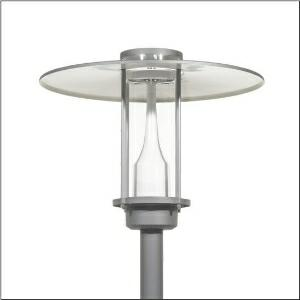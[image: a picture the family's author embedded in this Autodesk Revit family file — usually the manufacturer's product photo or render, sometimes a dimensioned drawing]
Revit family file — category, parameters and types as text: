
# Revit family: city-light_plus_iq___pl1_2s_5xa5275rf14h_8fc2
name_source: partatom
category: Lighting Fixtures
units: mm (PartAtom-declared; Revit-internal decimal feet)

## family parameters
Cut with Voids When Loaded = No
Host = Face
Light Source = No
Part Type = Normal
Room Calculation Point = No
Round Connector Dimension = Use Diameter
Shared = No

## types (1)
- --- (1 x LED, 2840 lm, 18.5 W, 4000K)
    Apparent Load = 19 VA
    CIE Flux Codes = 23 63 93 97 100
    Color Rendering = 70
    Color Temperature = 4000K
    Default Elevation = 1800 mm
    Description = City-Light Plus iQ, mast luminaire, Module 540 iQ-SR, primary light control with 3 zone facetted reflector, of plastic, silver coated, highly specular, structured, primary optical cover: cover, of PMMA, transparent, light distribution: PL1.2s, light emission: direct distribution, primary light characteristic: symmetric, installation type: post-top, LED, High Power LED, rated luminous flux: 2.840lm, luminous efficacy: 153lm/W, light colour: 740, colour temperature: 4000K, control gear: iQ Street-Remote, control: pre-setting: logarithmic dimming characteristic, Street-Remote, Auto-Match, Temp-Guard, Lumen-Switch, Night-Set, Smart-Wire, Light-Fading, Desk-Remote (wireless, voltage-free reading and setting of iQ features in the workshop via application-optimized NFC function/RFID function), optimised constant luminous flux control (CLO 2.0), with terminal, 6-pole, max. 2.5mm², mains connection: 230..240V, AC, 50/60Hz, start of lifetime: 19W, end of service life: 20W, reduction: 9W, luminaire housing, upper part, of glass-fibre reinforced polyester, coated, Siteco® metallic grey (DB 702S), diameter: 750mm, height: 590mm, spigot size: d x l = 76 x 70mm (post-top) | with reducer (optional accessory) 60 x 70mm, mounting height: 3..5m, post-top mast mounting element, of diecast aluminium, coated, Siteco® metallic grey (DB 702S), Module 540 iQ-SR, traffic white (RAL 9016), equipment: standard, protection rating (complete): IP65, insulation class (complete): insulation class II (safety insulation), certification: CE, ENEC, VDE, packaging unit: 1 piece

Light Distribution: PL1.2s
    Height = 590 mm
    Lamp = 1 x LED
    Lamp Light Flux = 2840 lm
    Lamp Power = 18.5 W
    Lamp count = 1
    Length = 750 mm
    Luminous efficacy = 154 lm/W
    Manufacturer = Siteco
    ModVariant = No
    Model = 5XA5275RF14H
    Number of Poles = 1
    OnlyDefault = Yes
    Power Factor = 1
    Product Name = City-Light Plus iQ | PL1.2s
    Product group = mast luminaire | pylon top
    ProductGroupID = 6100
    Protection Class = Protection class II
    Protection Degree = IP 65
    RLX_Detail_Level = 1
    RLX_Emergency_Light_Flux = 0 lm
    RLX_Emergency_Type = 0
    RLX_Emergency_Type_DB = No
    RlxData = <blob elided: 33277 chars, md5=73215785>
    Socket = socket
    Standby Power = 0 W
    System Light Flux = 2840 lm
    System Power = 19 W
    Type Comments = factory setting: luminous flux: 100 % | dim-lin: 254 | 385 mA
    Type Image = l_1006456.jpg
    URL = http://relux.com
    VarID = @adj_167001
    Voltage = 0 V
    Weight = 0.00 kg
    Width = 0 mm  [stored 0 ft]

note: [stored X ft] marks values corroborated as IEEE doubles in the binary element streams (Revit-internal decimal feet)

## geometry (parser evidence)
native form markers: Blend x4, Sweep x9
no freeform markers — native parametric forms only
